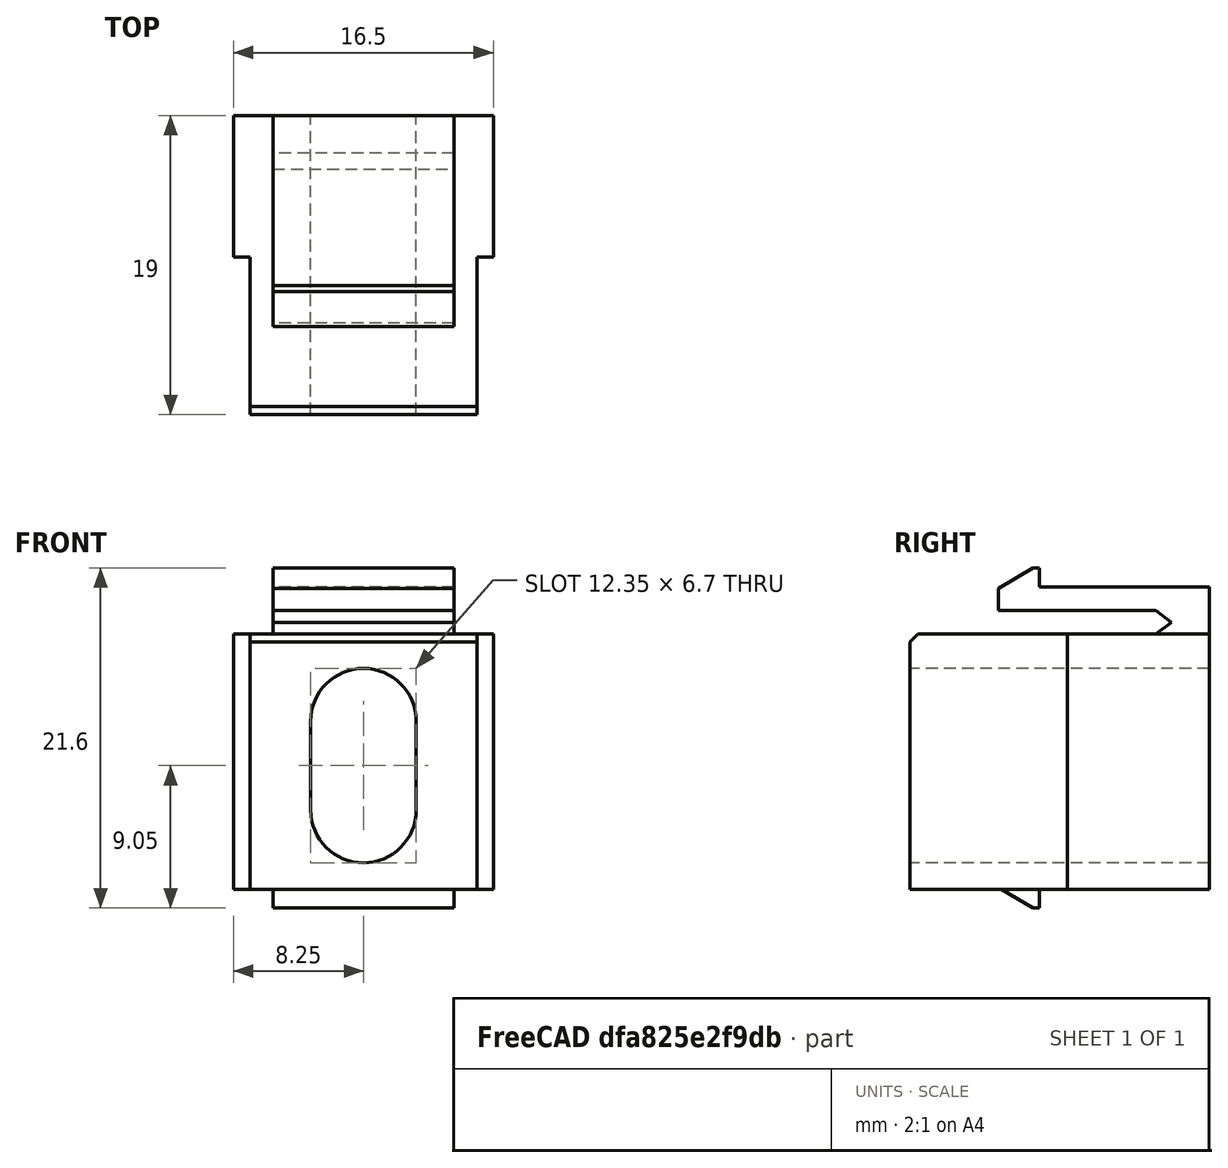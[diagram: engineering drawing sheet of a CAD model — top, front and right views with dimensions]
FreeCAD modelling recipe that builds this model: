
FCSTD DOCUMENT  (FreeCAD 1.0R39319 (Git))
Label: USB-C_Keystone
License: All rights reserved
LicenseURL: https://en.wikipedia.org/wiki/All_rights_reserved
objects: PartDesign::Pad×2, Part::Feature×1, PartDesign::FeatureBase×1, Sketcher::SketchObject×1, PartDesign::Pocket×1, PartDesign::Body×1, App::Part×1, App::FeaturePython×1, Assembly::JointGroup×1, Assembly::AssemblyObject×1
note: 15 computed .brp shape members not serialized (recipe doc carries the construction recipe); baked Part::Feature solids carry a one-line shape summary decoded from their .brp

FEATURE [Part::Feature] keystone_blank_insert_chamfer002_solid  label="keystone_blank_insert_chamfer002 (Solid)"
  shape: bbox 16.5 x 19 x 21.6 mm, 39 faces (baked)
FEATURE [PartDesign::FeatureBase] BaseFeature
  BaseFeature = -> keystone_blank_insert_chamfer002_solid
  Suppressed = false
FEATURE [PartDesign::Pad] Pad
  BaseFeature = -> BaseFeature
  Direction = (0,-1,0)
  Length = 10
  Length2 = 10
  Profile = -> BaseFeature [Face3]
  Refine = true
  Suppressed = false
  Type = 3
  UpToFace = -> BaseFeature [Face26]
FEATURE [PartDesign::Pad] Pad001
  BaseFeature = -> Pad
  Direction = (0,0,-1)
  Length = 10
  Length2 = 10
  Profile = -> Pad [Face11,Face14]
  Refine = true
  Suppressed = false
  Type = 3
  UpToFace = -> Pad [Face29]
FEATURE [Sketcher::SketchObject] Sketch
  ArcFitTolerance = 1e-06
  AttachmentSupport = -> [Pad001]
  ExternalGeometry = -> [Pad001]
  FullyConstrained = true
  MakeInternals = false
  MapMode = 5
  Placement = pos=(0,0,0) rot=(1,0,0;1.5708rad)
  sketch-geometry (8):
    g0: LineSegment [constr] StartX=0 StartY=0 StartZ=0 EndX=14.4 EndY=15.7 EndZ=0
    g1: ArcOfCircle CenterX=7.2 CenterY=10.675 CenterZ=0 NormalX=0 NormalY=0 NormalZ=1 AngleXU=0 Radius=3.35 StartAngle=4e-16 EndAngle=3.14159
    g2: ArcOfCircle CenterX=7.2 CenterY=5.025 CenterZ=0 NormalX=0 NormalY=0 NormalZ=1 AngleXU=0 Radius=3.35 StartAngle=3.14159 EndAngle=6.28319
    g3: LineSegment StartX=10.55 StartY=10.675 StartZ=0 EndX=10.55 EndY=5.025 EndZ=0
    g4: LineSegment StartX=3.85 StartY=10.675 StartZ=0 EndX=3.85 EndY=5.025 EndZ=0
    g5: LineSegment [constr] StartX=7.2 StartY=14.025 StartZ=0 EndX=7.2 EndY=1.675 EndZ=0
    g6: GeomPoint [constr] X=7.2 Y=7.85 Z=0
    g7: GeomPoint [constr] X=7.2 Y=7.85 Z=0
  constraints (17):
    c: Coincident(g0,g-1)
    c: Tangent(g1,g3) = 1.5708
    c: Tangent(g1,g4) = -1.5708
    c: Tangent(g2,g3) = 1.5708
    c: Tangent(g2,g4) = -1.5708
    c: Equal(g1,g2)
    c: Vertical(g3)
    c: Distance(g4,g3) = 6.7
    c: PointOnObject(g5,g1)
    c: PointOnObject(g5,g2)
    c: Vertical(g5)
    c: PointOnObject(g1,g5)
    c: DistanceY(g5,g5) = 12.35
    c: Symmetric(g0,g0,g6)
    c: Symmetric(g5,g5,g7)
    c: Coincident(g6,g7)
    c: Coincident(g-3,g0)
FEATURE [PartDesign::Pocket] Pocket
  BaseFeature = -> Pad001
  Direction = (0,1,-2e-16)
  Length = 5
  Length2 = 5
  Profile = -> Sketch
  ReferenceAxis = -> Sketch [N_Axis]
  Refine = true
  Suppressed = false
  Type = 1
FEATURE [PartDesign::Body] Body
  AllowCompound = false
  BaseFeature = -> keystone_blank_insert_chamfer002_solid
  Group = -> [BaseFeature,Pad,Pad001,Sketch,Pocket]
  Origin = -> Origin
  Tip = -> Pocket
FEATURE [App::Part] Part  label="Keystone"
  Group = -> [keystone_blank_insert_chamfer002_solid,Body]
  Origin = -> Origin001
FEATURE [App::FeaturePython] GroundedJoint  # Assembly grounded joint (typed FeaturePython)
  ObjectToGround = -> Part
FEATURE [Assembly::JointGroup] Joints
  Group = -> [GroundedJoint]
FEATURE [Assembly::AssemblyObject] Assembly  label="USB-C Keystone"
  Group = -> [Joints,Part,GroundedJoint]
  Origin = -> Origin004
  Type = Assembly
